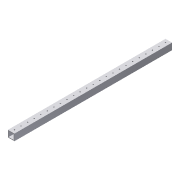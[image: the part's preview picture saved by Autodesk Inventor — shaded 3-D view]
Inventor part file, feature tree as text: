
AUTODESK INVENTOR PART (.ipt)
format: ipt  version: 2015 (Build 190159000, 159)  size: 129,536 bytes
history: native  units: in
note: dims shown in document units (in); Inventor stores cm internally (conversion verified against a paired STEP export)
features: sketch x2, extrude x1, hole x1, pattern_linear x1
ambient origin geometry x8: Origin, YZ Plane, XZ Plane, XY Plane, X Axis, Y Axis, Z Axis, Center Point
bodies: Solid1 (feature_tree)
feature tree (5):
  extrude  "Extrusion1"  Depth=1.0in
  hole  "Hole1"  [1 undecoded]
  pattern_linear  "Rectangular Pattern1"  Spacing1=0.5in  [1 undecoded]
  sketch  "Sketch1"  dims[d0=1.0in d1=1.0in]
  sketch  "Sketch2"  dims[d2=0.1in d4=0.0in d6=0.5in d7=0.164in d8=0.75in d9=0.375in d10=0.25in d11=0.5635in d12=1.0in d13=0.8108in d14=12.2047in d16=2.0in]
note: 2 required parameter values undecoded (feature->parameter linkage not recoverable at this tier; creation-order binding heuristic only, values carry confidence <= 0.55)
